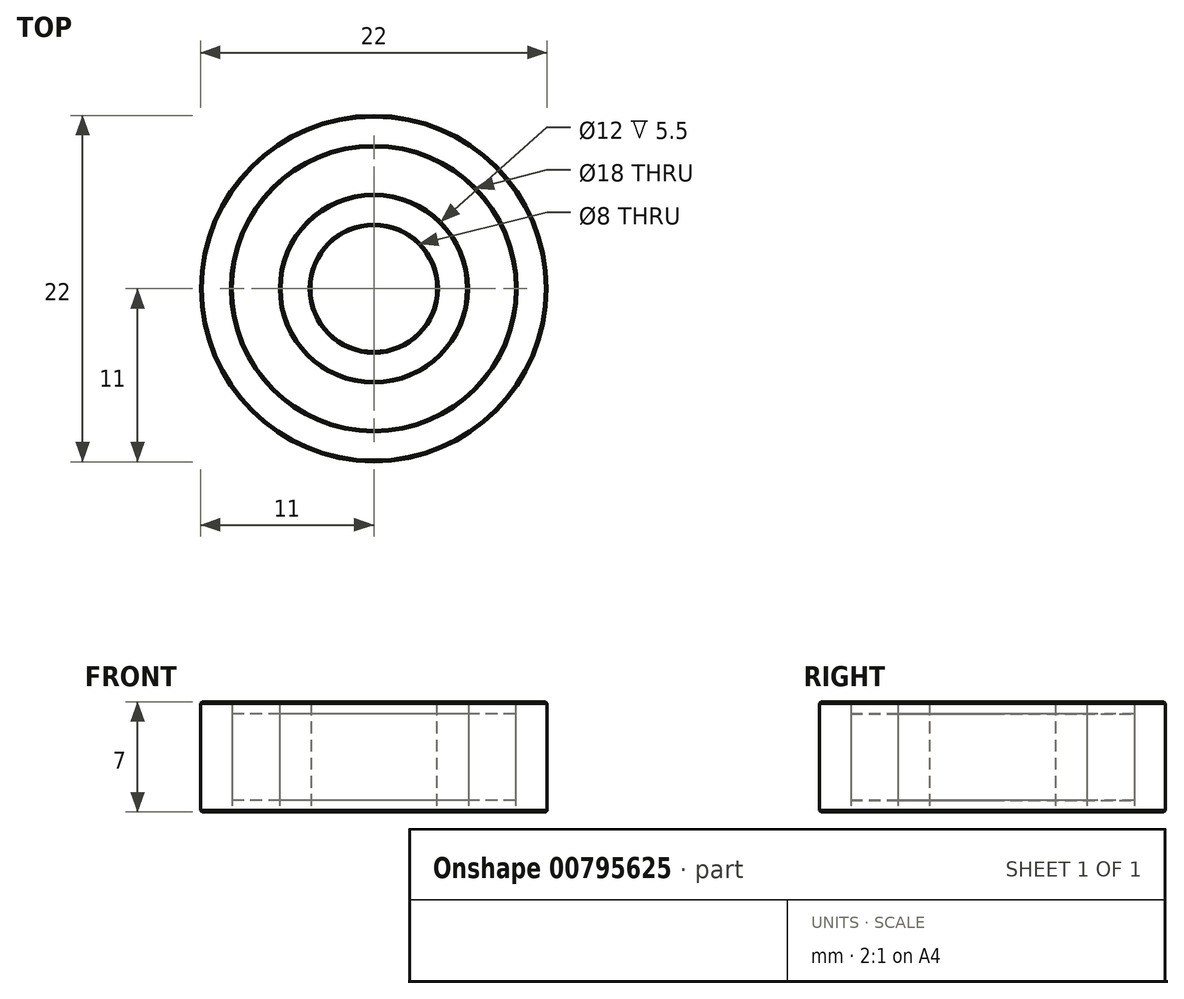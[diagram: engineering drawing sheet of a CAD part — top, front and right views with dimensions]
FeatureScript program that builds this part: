
annotation { "Feature Type Name" : "Feature", "Feature Type Description" : "" }
export const myFeature = defineFeature(function(context is Context, id is Id, definition is map)
    precondition{}
    {
        {
            var Q0;
            Q0=qCreatedBy(makeId("Top.planeOp"),FACE);
            var sketch = newSketch(context, id + "F0", { "sketchPlane" : qUnion([Q0])});
            skCircle(sketch, "E0", {"center": v(0, 0) * mm, "radius": 11 * mm});
            skCircle(sketch, "E1", {"center": v(0, 0) * mm, "radius": 4 * mm});
            skCircle(sketch, "E2", {"center": v(0, 0) * mm, "radius": 9 * mm});
            skCircle(sketch, "E3", {"center": v(0, 0) * mm, "radius": 6 * mm});
            skSolve(sketch);
        }
        {
            var Q0;
            Q0=makeQuery(id+"F0.imprint","IMPRINT",FACE,{"disambiguationData":[TD([[makeQuery(id+"F0.imprint","IMPRINT",EDGE,{"derivedFrom":sQuery(id+"F0.wireOp",EDGE,"E0")}),1.0]])]});
            var Q1;
            Q1=makeQuery(id+"F0.imprint","IMPRINT",FACE,{"disambiguationData":[TD([[makeQuery(id+"F0.imprint","IMPRINT",EDGE,{"derivedFrom":sQuery(id+"F0.wireOp",EDGE,"E1")}),-1.0]])]});
            extrude(context, id + "F1", {"entities" : qUnion([Q0, Q1]), "endBound" : BoundingType.SYMMETRIC, "depth" : 7 * mm, "offsetDistance" : 25 * mm});
        }
        {
            var Q0;
            Q0=makeQuery(id+"F0.imprint","IMPRINT",FACE,{"disambiguationData":[TD([[makeQuery(id+"F0.imprint","IMPRINT",EDGE,{"derivedFrom":sQuery(id+"F0.wireOp",EDGE,"E2")}),1.0]])]});
            extrude(context, id + "F2", {"entities" : qUnion([Q0]), "endBound" : BoundingType.SYMMETRIC, "depth" : 5.5 * mm, "offsetDistance" : 25 * mm});
        }
        {
            var Q0;
            Q0=makeQuery(id+"F1.opExtrude","CAP_EDGE",EDGE,{"disambiguationData":[OSD([sQuery(id+"F0.wireOp",EDGE,"E1")])],"isStart":false});
            var Q1;
            Q1=makeQuery(id+"F1.opExtrude","CAP_EDGE",EDGE,{"disambiguationData":[OSD([sQuery(id+"F0.wireOp",EDGE,"E1")])],"isStart":true});
            var Q2;
            Q2=makeQuery(id+"F1.opExtrude","CAP_EDGE",EDGE,{"disambiguationData":[OSD([sQuery(id+"F0.wireOp",EDGE,"E0")])],"isStart":false});
            var Q3;
            Q3=makeQuery(id+"F1.opExtrude","CAP_EDGE",EDGE,{"disambiguationData":[OSD([sQuery(id+"F0.wireOp",EDGE,"E2")])],"isStart":false});
            var Q4;
            Q4=makeQuery(id+"F1.opExtrude","CAP_EDGE",EDGE,{"disambiguationData":[OSD([sQuery(id+"F0.wireOp",EDGE,"E3")])],"isStart":false});
            var Q5;
            Q5=makeQuery(id+"F1.opExtrude","CAP_EDGE",EDGE,{"disambiguationData":[OSD([sQuery(id+"F0.wireOp",EDGE,"E0")])],"isStart":true});
            var Q6;
            Q6=makeQuery(id+"F1.opExtrude","CAP_EDGE",EDGE,{"disambiguationData":[OSD([sQuery(id+"F0.wireOp",EDGE,"E2")])],"isStart":true});
            var Q7;
            Q7=makeQuery(id+"F1.opExtrude","CAP_EDGE",EDGE,{"disambiguationData":[OSD([sQuery(id+"F0.wireOp",EDGE,"E3")])],"isStart":true});
            chamfer(context, id + "F3", {"entities" : qUnion([Q0, Q1, Q2, Q3, Q4, Q5, Q6, Q7]), "width" : 0.1 * mm, "tangentPropagation" : true});
        }
    });
